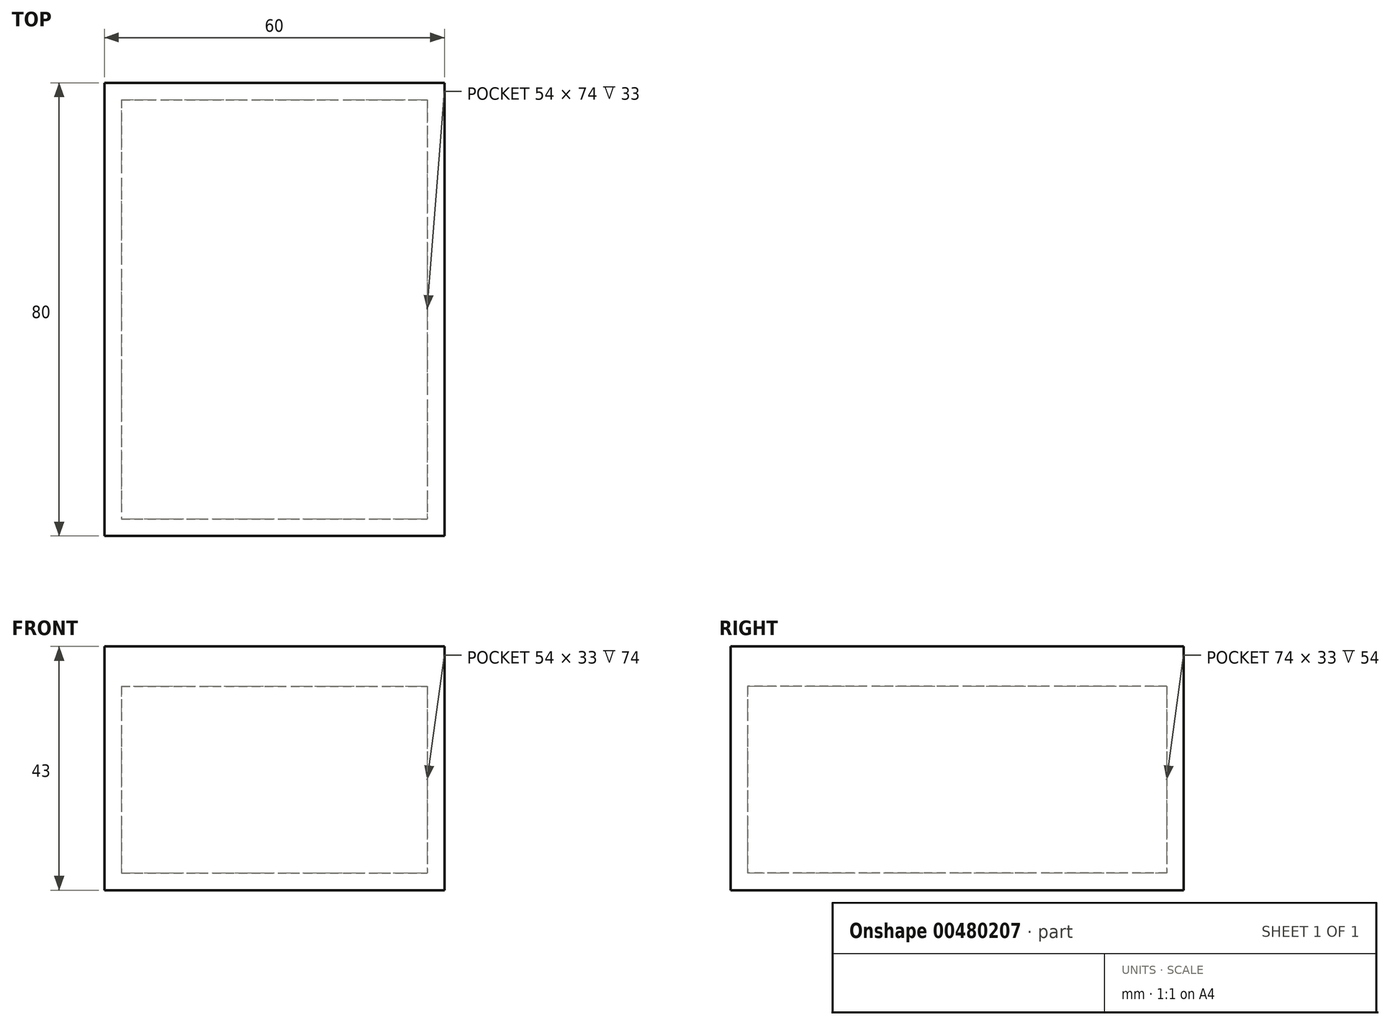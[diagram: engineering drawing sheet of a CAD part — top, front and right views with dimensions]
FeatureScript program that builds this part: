
annotation { "Feature Type Name" : "Feature", "Feature Type Description" : "" }
export const myFeature = defineFeature(function(context is Context, id is Id, definition is map)
    precondition{}
    {
        {
            var Q0;
            Q0=qCreatedBy(makeId("Top.planeOp"),FACE);
            var sketch = newSketch(context, id + "F0", { "sketchPlane" : qUnion([Q0])});
            skLineSegment(sketch, "E0.bottom", {"start": v(-30, 40) * mm, "end": v(30, 40) * mm});
            skLineSegment(sketch, "E0.top", {"start": v(-30, -40) * mm, "end": v(30, -40) * mm});
            skLineSegment(sketch, "E0.left", {"start": v(-30, 40) * mm, "end": v(-30, -40) * mm});
            skLineSegment(sketch, "E0.right", {"start": v(30, 40) * mm, "end": v(30, -40) * mm});
            skPoint(sketch, "E0.middle", {"position": v(0, 0) * mm});
            skSolve(sketch);
        }
        {
            var Q0;
            Q0=makeQuery(id+"F0.imprint","IMPRINT",FACE,{"disambiguationData":[TD([[makeQuery(id+"F0.imprint","IMPRINT",EDGE,{"derivedFrom":sQuery(id+"F0.wireOp",EDGE,"E0.bottom")}),-1.0]])]});
            extrude(context, id + "F1", {"entities" : qUnion([Q0]), "depth" : 40 * mm});
        }
        {
            var Q0;
            Q0=makeQuery(id+"F1.opExtrude","CAP_FACE",FACE,{"disambiguationData":[OSD([sQuery(id+"F0.wireOp",EDGE,"E0.bottom"),sQuery(id+"F0.wireOp",EDGE,"E0.top"),sQuery(id+"F0.wireOp",EDGE,"E0.left"),sQuery(id+"F0.wireOp",EDGE,"E0.right")])],"isStart":false});
            shell(context, id + "F2", {"entities" : qUnion([Q0]), "thickness" : 3 * mm});
        }
        {
            var Q0;
            Q0=makeQuery(id+"F1.opExtrude","CAP_FACE",FACE,{"disambiguationData":[OSD([sQuery(id+"F0.wireOp",EDGE,"E0.bottom"),sQuery(id+"F0.wireOp",EDGE,"E0.top"),sQuery(id+"F0.wireOp",EDGE,"E0.left"),sQuery(id+"F0.wireOp",EDGE,"E0.right")])],"isStart":false});
            var sketch = newSketch(context, id + "F3", { "sketchPlane" : qUnion([Q0])});
            skLineSegment(sketch, "E1.bottom", {"start": v(-30, 40) * mm, "end": v(30, 40) * mm});
            skLineSegment(sketch, "E1.top", {"start": v(-30, -40) * mm, "end": v(30, -40) * mm});
            skLineSegment(sketch, "E1.left", {"start": v(-30, 40) * mm, "end": v(-30, -40) * mm});
            skLineSegment(sketch, "E1.right", {"start": v(30, 40) * mm, "end": v(30, -40) * mm});
            skLineSegment(sketch, "E2.bottom", {"start": v(-27, 37) * mm, "end": v(27, 37) * mm});
            skLineSegment(sketch, "E2.top", {"start": v(-27, -37) * mm, "end": v(27, -37) * mm});
            skLineSegment(sketch, "E2.left", {"start": v(-27, 37) * mm, "end": v(-27, -37) * mm});
            skLineSegment(sketch, "E2.right", {"start": v(27, 37) * mm, "end": v(27, -37) * mm});
            skSolve(sketch);
        }
        {
            var Q0;
            Q0=makeQuery(id+"F3.imprint","IMPRINT",FACE,{"disambiguationData":[TD([[makeQuery(id+"F3.imprint","IMPRINT",EDGE,{"derivedFrom":sQuery(id+"F3.wireOp",EDGE,"E1.bottom")}),-1.0]])]});
            var Q1;
            Q1=makeQuery(id+"F3.imprint","IMPRINT",FACE,{"disambiguationData":[TD([[makeQuery(id+"F3.imprint","IMPRINT",EDGE,{"derivedFrom":sQuery(id+"F3.wireOp",EDGE,"E2.bottom")}),-1.0]])]});
            extrude(context, id + "F4", {"entities" : qUnion([Q0, Q1]), "depth" : 3 * mm});
        }
        {
            var Q0;
            Q0=makeQuery(id+"F3.imprint","IMPRINT",FACE,{"disambiguationData":[TD([[makeQuery(id+"F3.imprint","IMPRINT",EDGE,{"derivedFrom":sQuery(id+"F3.wireOp",EDGE,"E2.bottom")}),-1.0]])]});
            extrude(context, id + "F5", {"entities" : qUnion([Q0]), "operationType" : NewBodyOperationType.ADD, "oppositeDirection" : true, "depth" : 4 * mm});
        }
    });
